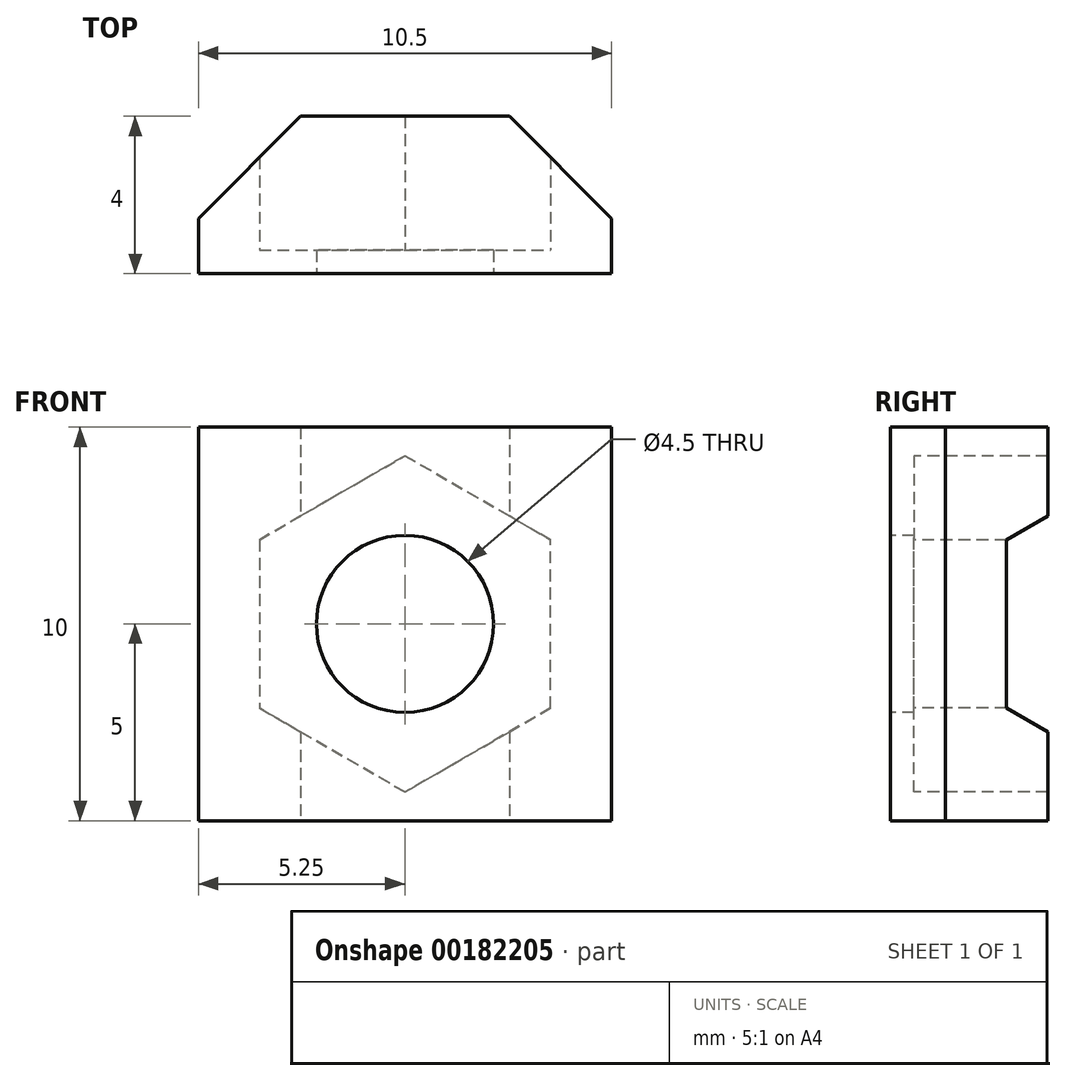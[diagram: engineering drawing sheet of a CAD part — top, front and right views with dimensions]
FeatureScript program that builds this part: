
annotation { "Feature Type Name" : "Feature", "Feature Type Description" : "" }
export const myFeature = defineFeature(function(context is Context, id is Id, definition is map)
    precondition{}
    {
        {
            var Q0;
            Q0=qCreatedBy(makeId("Top.planeOp"),FACE);
            var sketch = newSketch(context, id + "F0", { "sketchPlane" : qUnion([Q0])});
            skLineSegment(sketch, "E0", {"start": v(0, 0) * mm, "end": v(10.5, 0) * mm});
            skLineSegment(sketch, "E1", {"start": v(10.5, 0) * mm, "end": v(10.5, 1.4) * mm});
            skLineSegment(sketch, "E2", {"start": v(10.5, 1.4) * mm, "end": v(7.9, 4) * mm});
            skLineSegment(sketch, "E3", {"start": v(7.9, 4) * mm, "end": v(2.6, 4) * mm});
            skLineSegment(sketch, "E4", {"start": v(2.6, 4) * mm, "end": v(0, 1.4) * mm});
            skLineSegment(sketch, "E5", {"start": v(0, 1.4) * mm, "end": v(0, 0) * mm});
            skSolve(sketch);
        }
        {
            var Q0;
            Q0=makeQuery(id+"F0.imprint","IMPRINT",FACE,{"disambiguationData":[TD([[makeQuery(id+"F0.imprint","IMPRINT",EDGE,{"derivedFrom":sQuery(id+"F0.wireOp",EDGE,"E0")}),1.0]])]});
            extrude(context, id + "F1", {"entities" : qUnion([Q0]), "depth" : 10 * mm});
        }
        {
            var Q0;
            Q0=makeQuery(id+"F1.opExtrude","SWEPT_FACE",FACE,{"disambiguationData":[OSD([sQuery(id+"F0.wireOp",EDGE,"E0")])]});
            var sketch = newSketch(context, id + "F2", { "sketchPlane" : qUnion([Q0])});
            skCircle(sketch, "E6.cCircle", {"center": v(5.25, 5) * mm, "radius": 3.7 * mm, "construction": true});
            skPoint(sketch, "E6.cCircle.centerSnap0", {"position": v(5.25, 0) * mm});
            skPoint(sketch, "E6.cCircle.centerSnap1", {"position": v(10.5, 5) * mm});
            skPoint(sketch, "E6.cCircle.perimeterSnap0", {"position": v(10.5, 5) * mm});
            skLineSegment(sketch, "E6.0", {"start": v(8.95, 7.14) * mm, "end": v(8.95, 2.86) * mm});
            skLineSegment(sketch, "E6.1", {"start": v(8.95, 2.86) * mm, "end": v(5.25, 0.73) * mm});
            skLineSegment(sketch, "E6.2", {"start": v(5.25, 0.73) * mm, "end": v(1.55, 2.86) * mm});
            skLineSegment(sketch, "E6.3", {"start": v(1.55, 2.86) * mm, "end": v(1.55, 7.14) * mm});
            skLineSegment(sketch, "E6.4", {"start": v(1.55, 7.14) * mm, "end": v(5.25, 9.27) * mm});
            skLineSegment(sketch, "E6.5", {"start": v(5.25, 9.27) * mm, "end": v(8.95, 7.14) * mm});
            skPoint(sketch, "E6.0.midPoint", {"position": v(8.95, 5) * mm});
            skPoint(sketch, "E6.0.midPoint.positionSnap0", {"position": v(10.5, 5) * mm});
            skCircle(sketch, "E7", {"center": v(5.25, 5) * mm, "radius": 2.25 * mm});
            skSolve(sketch);
        }
        {
            var Q0;
            Q0=makeQuery(id+"F2.imprint","IMPRINT",FACE,{"disambiguationData":[TD([[makeQuery(id+"F2.imprint","IMPRINT",EDGE,{"derivedFrom":sQuery(id+"F2.wireOp",EDGE,"E6.0")}),-1.0]])]});
            var Q1;
            Q1=makeQuery(id+"F2.imprint","IMPRINT",FACE,{"disambiguationData":[TD([[makeQuery(id+"F2.imprint","IMPRINT",EDGE,{"derivedFrom":sQuery(id+"F2.wireOp",EDGE,"E7")}),1.0]])]});
            extrude(context, id + "F3", {"entities" : qUnion([Q0, Q1]), "operationType" : NewBodyOperationType.REMOVE, "endBound" : BoundingType.UP_TO_NEXT, "oppositeDirection" : true, "depth" : 25 * mm, "hasSecondDirection" : true, "secondDirectionOppositeDirection" : true, "secondDirectionDepth" : 0.6 * mm});
        }
        {
            var Q0;
            Q0=makeQuery(id+"F2.imprint","IMPRINT",FACE,{"disambiguationData":[TD([[makeQuery(id+"F2.imprint","IMPRINT",EDGE,{"derivedFrom":sQuery(id+"F2.wireOp",EDGE,"E7")}),1.0]])]});
            extrude(context, id + "F4", {"entities" : qUnion([Q0]), "operationType" : NewBodyOperationType.REMOVE, "endBound" : BoundingType.UP_TO_NEXT, "oppositeDirection" : true, "depth" : 25 * mm});
        }
    });
